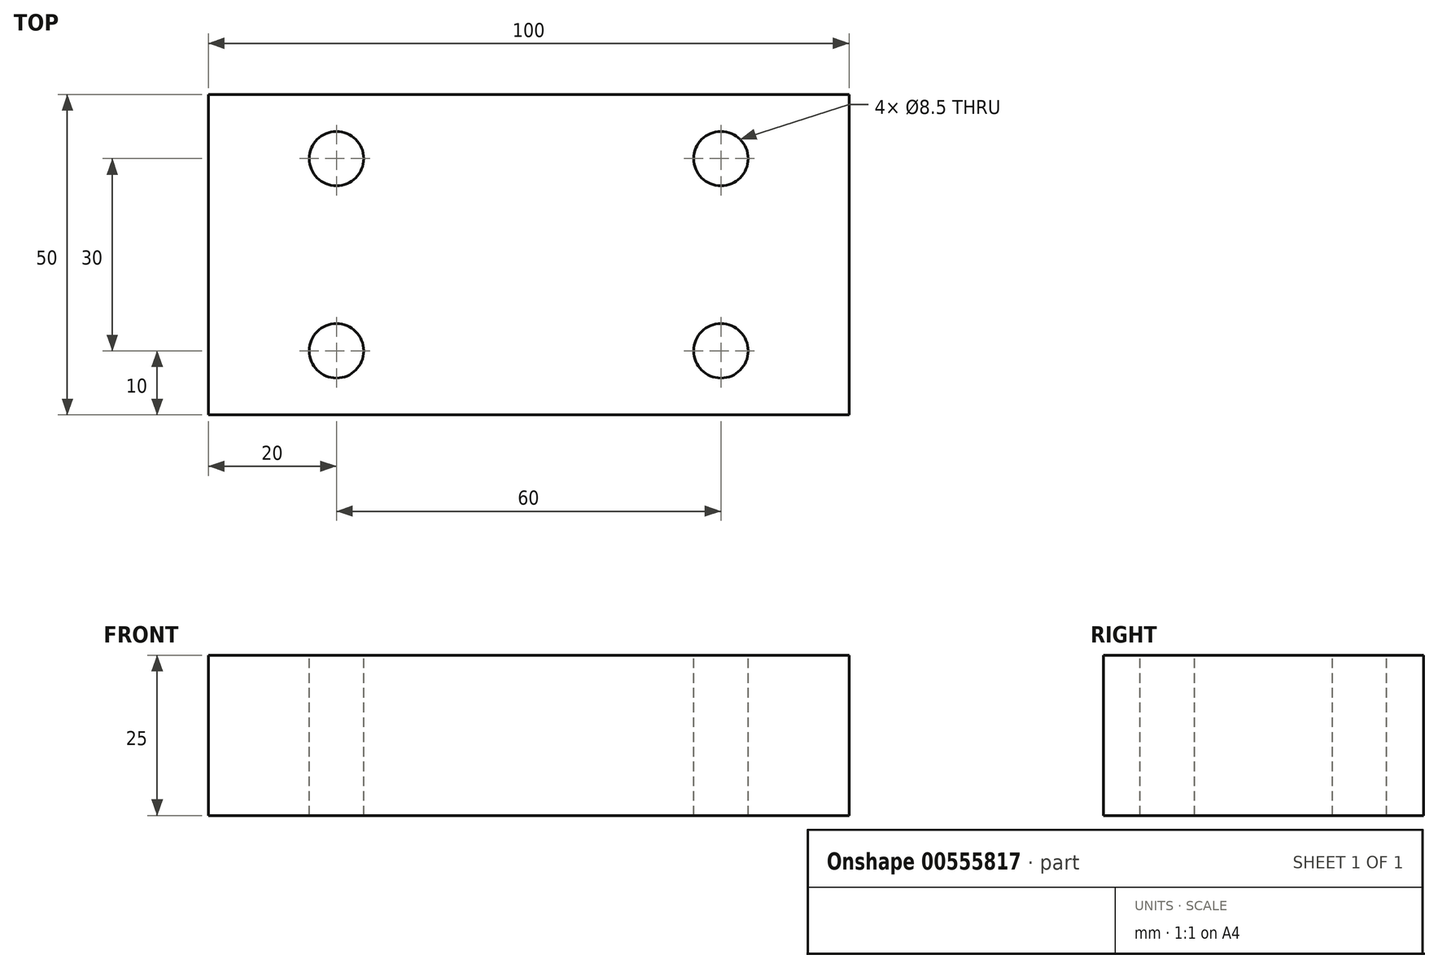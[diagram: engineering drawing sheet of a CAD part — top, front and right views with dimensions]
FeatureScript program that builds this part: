
annotation { "Feature Type Name" : "Feature", "Feature Type Description" : "" }
export const myFeature = defineFeature(function(context is Context, id is Id, definition is map)
    precondition{}
    {
        {
            var Q0;
            Q0=qCreatedBy(makeId("Top.planeOp"),FACE);
            var sketch = newSketch(context, id + "F0", { "sketchPlane" : qUnion([Q0])});
            skLineSegment(sketch, "E0.bottom", {"start": v(0, 0) * mm, "end": v(100, 0) * mm});
            skLineSegment(sketch, "E0.top", {"start": v(0, 50) * mm, "end": v(100, 50) * mm});
            skLineSegment(sketch, "E0.left", {"start": v(0, 0) * mm, "end": v(0, 50) * mm});
            skLineSegment(sketch, "E0.right", {"start": v(100, 0) * mm, "end": v(100, 50) * mm});
            skSolve(sketch);
        }
        {
            var Q0;
            Q0=makeQuery(id+"F0.imprint","IMPRINT",FACE,{"disambiguationData":[TD([[makeQuery(id+"F0.imprint","IMPRINT",EDGE,{"derivedFrom":sQuery(id+"F0.wireOp",EDGE,"E0.bottom")}),1.0]])]});
            extrude(context, id + "F1", {"entities" : qUnion([Q0]), "depth" : 25 * mm, "offsetDistance" : 25 * mm});
        }
        {
            var Q0;
            Q0=makeQuery(id+"F1.opExtrude","CAP_FACE",FACE,{"disambiguationData":[OSD([sQuery(id+"F0.wireOp",EDGE,"E0.bottom"),sQuery(id+"F0.wireOp",EDGE,"E0.top"),sQuery(id+"F0.wireOp",EDGE,"E0.left"),sQuery(id+"F0.wireOp",EDGE,"E0.right")])],"isStart":false});
            var sketch = newSketch(context, id + "F2", { "sketchPlane" : qUnion([Q0])});
            skPoint(sketch, "E1", {"position": v(20, 40) * mm});
            skPoint(sketch, "E2", {"position": v(80, 40) * mm});
            skPoint(sketch, "E3", {"position": v(80, 10) * mm});
            skPoint(sketch, "E4", {"position": v(20, 10) * mm});
            skLineSegment(sketch, "E5", {"start": v(0, 25) * mm, "end": v(100, 25) * mm});
            skLineSegment(sketch, "E6", {"start": v(50, 50) * mm, "end": v(50, 0) * mm});
            skSolve(sketch);
        }
        {
            var Q0;
            Q0=sQuery(id+"F2.wireOp",VERTEX,"E4");
            var Q1;
            Q1=sQuery(id+"F2.wireOp",VERTEX,"E1");
            var Q2;
            Q2=sQuery(id+"F2.wireOp",VERTEX,"E2");
            var Q3;
            Q3=sQuery(id+"F2.wireOp",VERTEX,"E3");
            var Q4;
            Q4=makeQuery(id+"F1.opExtrude","SWEPT_BODY",BODY,{"disambiguationData":[OSD([sQuery(id+"F0.wireOp",EDGE,"E0.bottom"),sQuery(id+"F0.wireOp",EDGE,"E0.top"),sQuery(id+"F0.wireOp",EDGE,"E0.left"),sQuery(id+"F0.wireOp",EDGE,"E0.right")])]});
            hole(context, id + "F3", {"style" : HoleStyle.SIMPLE, "endStyle" : HoleEndStyle.THROUGH, "standardTappedOrClearance" : lookupTablePath({ "standard" : "ISO", "engagement" : "75%", "pitch" : "1.5 mm", "size" : "M10", "type" : "Tapped" }), "standardBlindInLast" : lookupTablePath({ "standard" : "ISO", "engagement" : "75%", "pitch" : "1.5 mm", "size" : "M10", "type" : "Tapped" }), "holeDiameter" : 8.5 * mm, "showTappedDepth" : true, "isTappedThrough" : true, "tappedDepth" : 12 * mm, "tapClearance" : 3, "locations" : qUnion([Q0, Q1, Q2, Q3]), "scope" : qUnion([Q4]), "majorDiameter" : 10 * mm});
        }
    });
